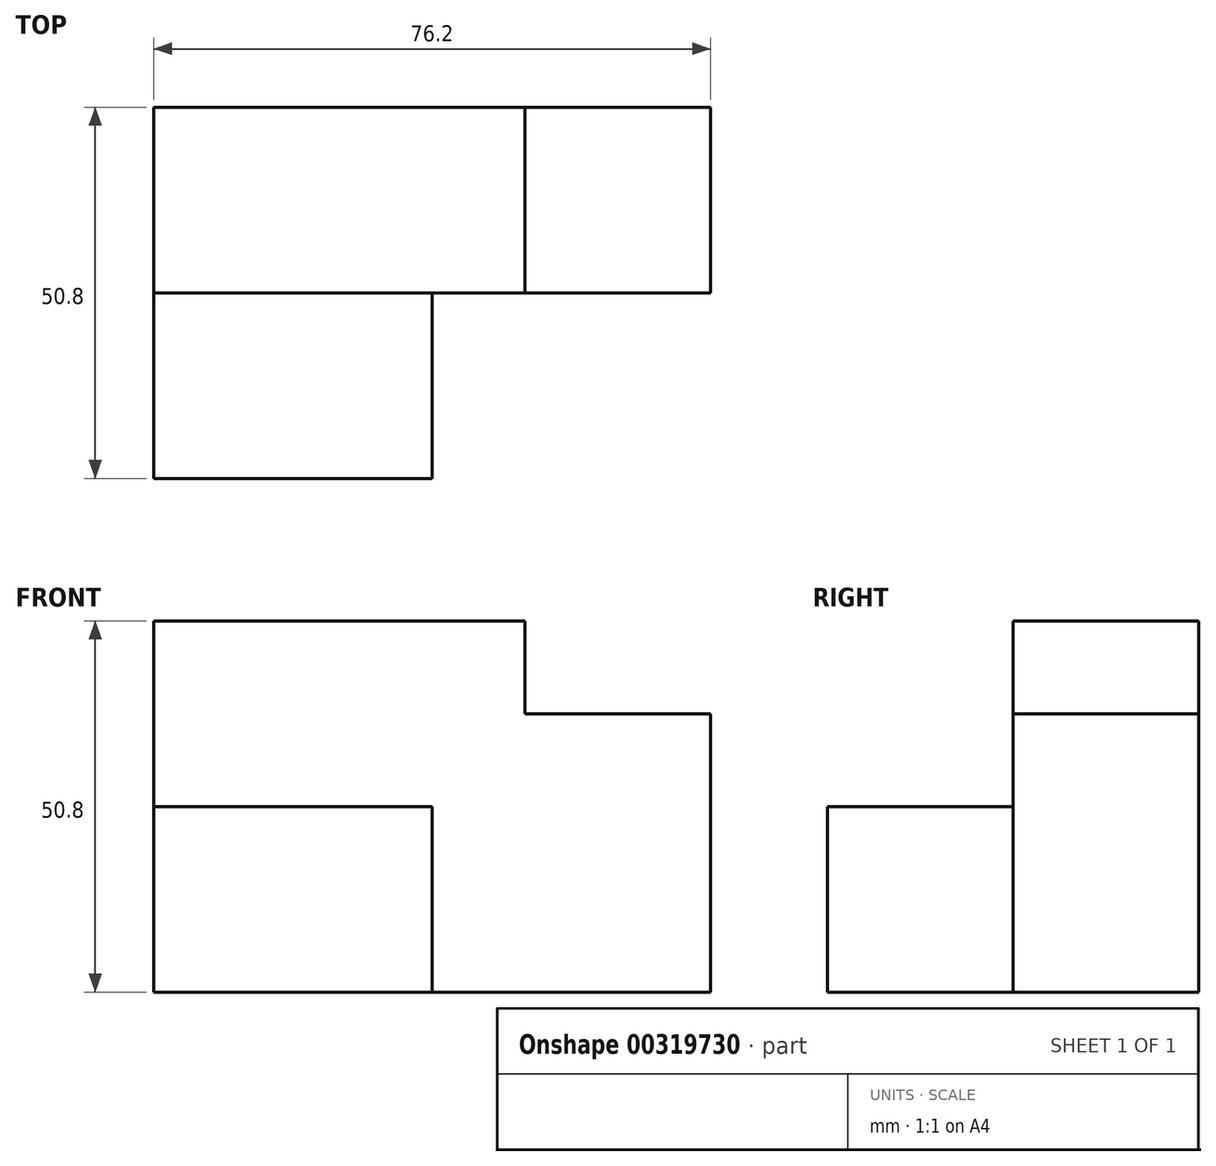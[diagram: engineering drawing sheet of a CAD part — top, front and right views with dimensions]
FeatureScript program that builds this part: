
annotation { "Feature Type Name" : "Feature", "Feature Type Description" : "" }
export const myFeature = defineFeature(function(context is Context, id is Id, definition is map)
    precondition{}
    {
        {
            var Q0;
            Q0=qCreatedBy(makeId("Front.planeOp"),FACE);
            var sketch = newSketch(context, id + "F0", { "sketchPlane" : qUnion([Q0])});
            skLineSegment(sketch, "E0", {"start": v(-36.32, -31.75) * mm, "end": v(-36.32, -57.15) * mm});
            skLineSegment(sketch, "E1", {"start": v(-36.32, -57.15) * mm, "end": v(1.78, -57.15) * mm});
            skLineSegment(sketch, "E2", {"start": v(1.78, -57.15) * mm, "end": v(1.78, -31.75) * mm});
            skLineSegment(sketch, "E3", {"start": v(1.78, -31.75) * mm, "end": v(-36.32, -31.75) * mm});
            skLineSegment(sketch, "E4", {"start": v(-36.32, -31.75) * mm, "end": v(-36.32, -6.35) * mm});
            skLineSegment(sketch, "E5", {"start": v(-36.32, -6.35) * mm, "end": v(14.48, -6.35) * mm});
            skLineSegment(sketch, "E6", {"start": v(14.48, -6.35) * mm, "end": v(14.48, -19.05) * mm});
            skLineSegment(sketch, "E7", {"start": v(14.48, -19.05) * mm, "end": v(39.88, -19.05) * mm});
            skLineSegment(sketch, "E8", {"start": v(39.88, -19.05) * mm, "end": v(39.88, -57.15) * mm});
            skLineSegment(sketch, "E9", {"start": v(39.88, -57.15) * mm, "end": v(1.78, -57.15) * mm});
            skSolve(sketch);
        }
        {
            var Q0;
            Q0=makeQuery(id+"F0.imprint","IMPRINT",FACE,{"disambiguationData":[TD([[makeQuery(id+"F0.imprint","IMPRINT",EDGE,{"derivedFrom":sQuery(id+"F0.wireOp",EDGE,"E2")}),-1.0]])]});
            var Q1;
            Q1=makeQuery(id+"F0.imprint","IMPRINT",FACE,{"disambiguationData":[TD([[makeQuery(id+"F0.imprint","IMPRINT",EDGE,{"derivedFrom":sQuery(id+"F0.wireOp",EDGE,"E0")}),1.0]])]});
            extrude(context, id + "F1", {"entities" : qUnion([Q0, Q1]), "oppositeDirection" : true, "depth" : 25.4 * mm});
        }
        {
            var Q0;
            Q0=makeQuery(id+"F0.imprint","IMPRINT",FACE,{"disambiguationData":[TD([[makeQuery(id+"F0.imprint","IMPRINT",EDGE,{"derivedFrom":sQuery(id+"F0.wireOp",EDGE,"E0")}),1.0]])]});
            extrude(context, id + "F2", {"entities" : qUnion([Q0]), "operationType" : NewBodyOperationType.ADD, "depth" : 25.4 * mm});
        }
    });
